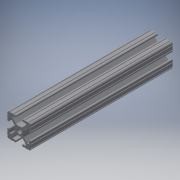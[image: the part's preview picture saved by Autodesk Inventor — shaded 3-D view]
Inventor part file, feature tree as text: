
AUTODESK INVENTOR PART (.ipt)
format: ipt  version: 2018 (Build 220112000, 112)  size: 226,304 bytes
history: native  units: in
note: dims shown in document units (in); Inventor stores cm internally (conversion verified against a paired STEP export)
features: extrude x1, sketch x1
ambient origin geometry x8: Origin, YZ Plane, XZ Plane, XY Plane, X Axis, Y Axis, Z Axis, Center Point
bodies: Solid1 (feature_tree)
feature tree (2):
  extrude  "Extrusion1"  [1 undecoded]
  sketch  "Sketch1"  dims[d0=6.0in d1=0.0in]
note: 1 required parameter value undecoded (feature->parameter linkage not recoverable at this tier; creation-order binding heuristic only, values carry confidence <= 0.55)
